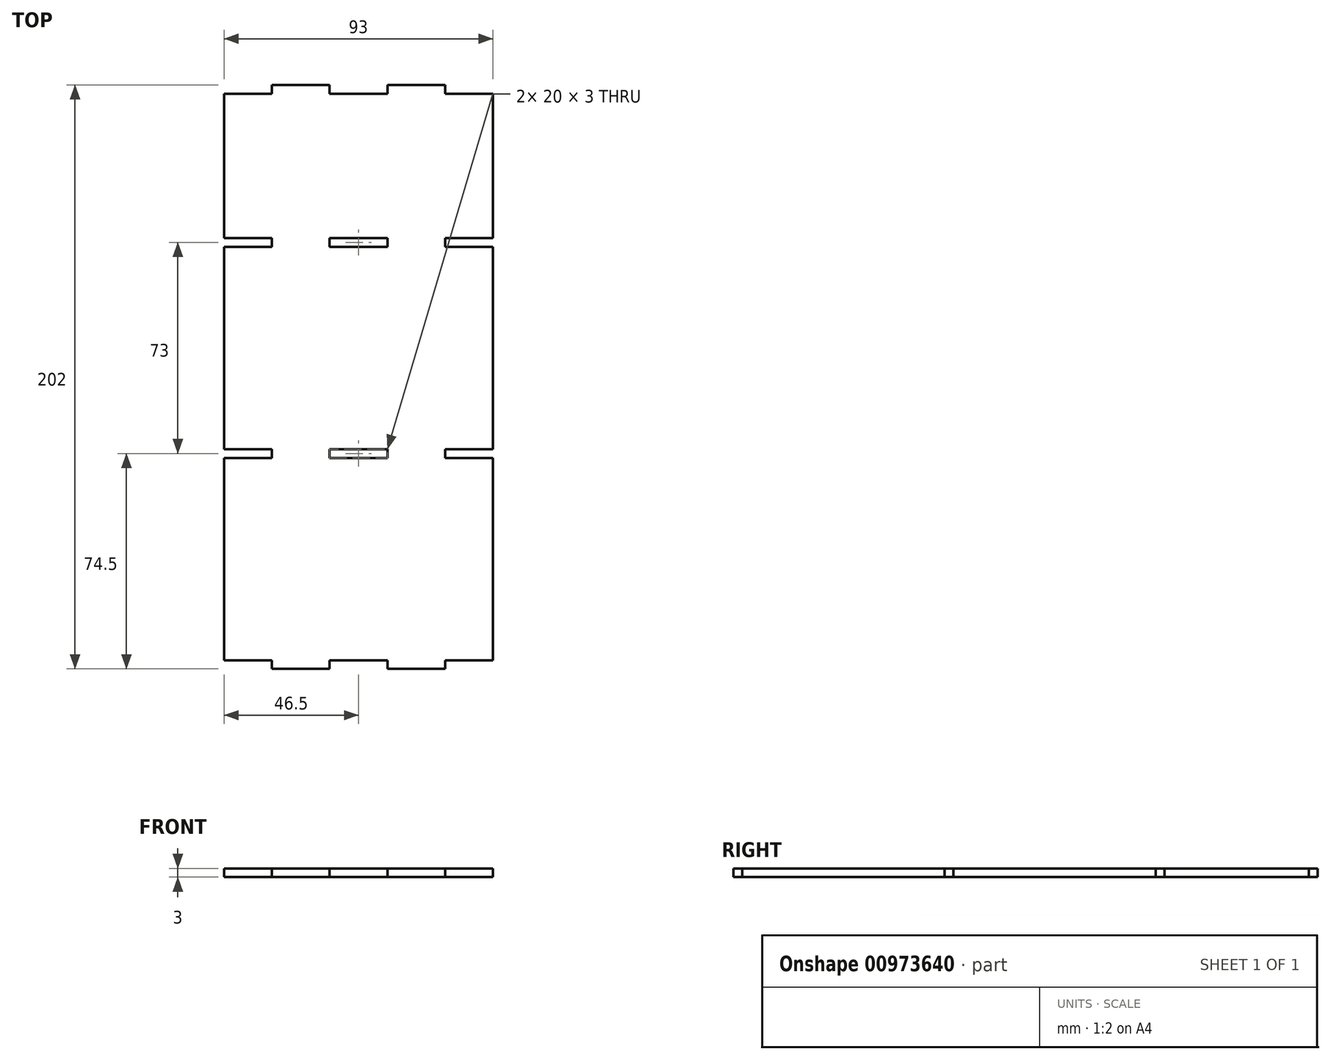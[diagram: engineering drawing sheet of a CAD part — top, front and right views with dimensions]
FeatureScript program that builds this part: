
annotation { "Feature Type Name" : "Feature", "Feature Type Description" : "" }
export const myFeature = defineFeature(function(context is Context, id is Id, definition is map)
    precondition{}
    {
        {
            var Q0;
            Q0=qCreatedBy(makeId("Top.planeOp"),FACE);
            var sketch = newSketch(context, id + "F0", { "sketchPlane" : qUnion([Q0])});
            skLineSegment(sketch, "E0", {"start": v(0, 0) * mm, "end": v(100, 0) * mm});
            skLineSegment(sketch, "E1", {"start": v(100, 0) * mm, "end": v(100, -202) * mm});
            skLineSegment(sketch, "E2", {"start": v(100, -202) * mm, "end": v(0, -202) * mm});
            skLineSegment(sketch, "E3", {"start": v(0, -202) * mm, "end": v(0, 0) * mm});
            skLineSegment(sketch, "E4", {"start": v(0, 0) * mm, "end": v(0, -3) * mm});
            skLineSegment(sketch, "E5", {"start": v(0, -3) * mm, "end": v(20, -3) * mm});
            skLineSegment(sketch, "E6", {"start": v(20, -3) * mm, "end": v(20, 0) * mm});
            skLineSegment(sketch, "E7", {"start": v(20, 0) * mm, "end": v(40, 0) * mm});
            skLineSegment(sketch, "E8", {"start": v(40, 0) * mm, "end": v(40, -3) * mm});
            skLineSegment(sketch, "E9", {"start": v(40, -3) * mm, "end": v(60, -3) * mm});
            skLineSegment(sketch, "E10", {"start": v(60, -3) * mm, "end": v(60, 0) * mm});
            skLineSegment(sketch, "E11", {"start": v(60, 0) * mm, "end": v(80, 0) * mm});
            skLineSegment(sketch, "E12", {"start": v(80, 0) * mm, "end": v(80, -3) * mm});
            skLineSegment(sketch, "E13", {"start": v(80, -3) * mm, "end": v(100, -3) * mm});
            skLineSegment(sketch, "E14", {"start": v(0, -202) * mm, "end": v(0, -199) * mm});
            skLineSegment(sketch, "E15", {"start": v(0, -199) * mm, "end": v(20, -199) * mm});
            skLineSegment(sketch, "E16", {"start": v(20, -199) * mm, "end": v(20, -202) * mm});
            skLineSegment(sketch, "E17", {"start": v(20, -202) * mm, "end": v(40, -202) * mm});
            skLineSegment(sketch, "E18", {"start": v(40, -202) * mm, "end": v(40, -199) * mm});
            skLineSegment(sketch, "E19", {"start": v(40, -199) * mm, "end": v(60, -199) * mm});
            skLineSegment(sketch, "E20", {"start": v(60, -199) * mm, "end": v(60, -202) * mm});
            skLineSegment(sketch, "E21", {"start": v(60, -202) * mm, "end": v(80, -202) * mm});
            skLineSegment(sketch, "E22", {"start": v(80, -202) * mm, "end": v(80, -199) * mm});
            skLineSegment(sketch, "E23", {"start": v(80, -199) * mm, "end": v(100, -199) * mm});
            skLineSegment(sketch, "E24", {"start": v(0, -3) * mm, "end": v(0, -53) * mm});
            skLineSegment(sketch, "E25", {"start": v(0, -53) * mm, "end": v(20, -53) * mm});
            skLineSegment(sketch, "E26", {"start": v(20, -53) * mm, "end": v(20, -56) * mm});
            skLineSegment(sketch, "E27", {"start": v(20, -56) * mm, "end": v(0, -56) * mm});
            skLineSegment(sketch, "E28", {"start": v(0, -56) * mm, "end": v(0, -126) * mm});
            skLineSegment(sketch, "E29", {"start": v(0, -126) * mm, "end": v(20, -126) * mm});
            skLineSegment(sketch, "E30", {"start": v(20, -126) * mm, "end": v(20, -129) * mm});
            skLineSegment(sketch, "E31", {"start": v(20, -129) * mm, "end": v(0, -129) * mm});
            skLineSegment(sketch, "E32", {"start": v(100, -3) * mm, "end": v(100, -53) * mm});
            skLineSegment(sketch, "E33", {"start": v(100, -53) * mm, "end": v(80, -53) * mm});
            skLineSegment(sketch, "E34", {"start": v(80, -53) * mm, "end": v(80, -56) * mm});
            skLineSegment(sketch, "E35", {"start": v(80, -56) * mm, "end": v(100, -56) * mm});
            skLineSegment(sketch, "E36", {"start": v(100, -56) * mm, "end": v(100, -126) * mm});
            skLineSegment(sketch, "E37", {"start": v(100, -126) * mm, "end": v(80, -126) * mm});
            skLineSegment(sketch, "E38", {"start": v(80, -126) * mm, "end": v(80, -129) * mm});
            skLineSegment(sketch, "E39", {"start": v(80, -129) * mm, "end": v(100, -129) * mm});
            skLineSegment(sketch, "E40", {"start": v(40, -53) * mm, "end": v(60, -53) * mm});
            skLineSegment(sketch, "E41", {"start": v(60, -53) * mm, "end": v(60, -56) * mm});
            skLineSegment(sketch, "E42", {"start": v(60, -56) * mm, "end": v(40, -56) * mm});
            skLineSegment(sketch, "E43", {"start": v(40, -56) * mm, "end": v(40, -53) * mm});
            skLineSegment(sketch, "E44", {"start": v(40, -126) * mm, "end": v(60, -126) * mm});
            skLineSegment(sketch, "E45", {"start": v(60, -126) * mm, "end": v(60, -129) * mm});
            skLineSegment(sketch, "E46", {"start": v(60, -129) * mm, "end": v(40, -129) * mm});
            skLineSegment(sketch, "E47", {"start": v(40, -129) * mm, "end": v(40, -126) * mm});
            skLineSegment(sketch, "E48", {"start": v(0, -3) * mm, "end": v(3.5, -3) * mm});
            skLineSegment(sketch, "E49", {"start": v(3.5, -3) * mm, "end": v(3.5, -199) * mm});
            skLineSegment(sketch, "E50", {"start": v(100, -3) * mm, "end": v(96.5, -3) * mm});
            skLineSegment(sketch, "E51", {"start": v(96.5, -3) * mm, "end": v(96.5, -199) * mm});
            skSolve(sketch);
        }
        {
            var Q0;
            {var subQ27=sQuery(id+"F0.wireOp",EDGE,"E6");Q0=makeQuery(id+"F0.imprint","IMPRINT",FACE,{"disambiguationData":[TD([[makeQuery(id+"F0.imprint","IMPRINT",EDGE,{"derivedFrom":subQ27}),-1.0]])]});}
            extrude(context, id + "F1", {"entities" : qUnion([Q0]), "depth" : 3 * mm, "offsetDistance" : 25 * mm});
        }
    });
